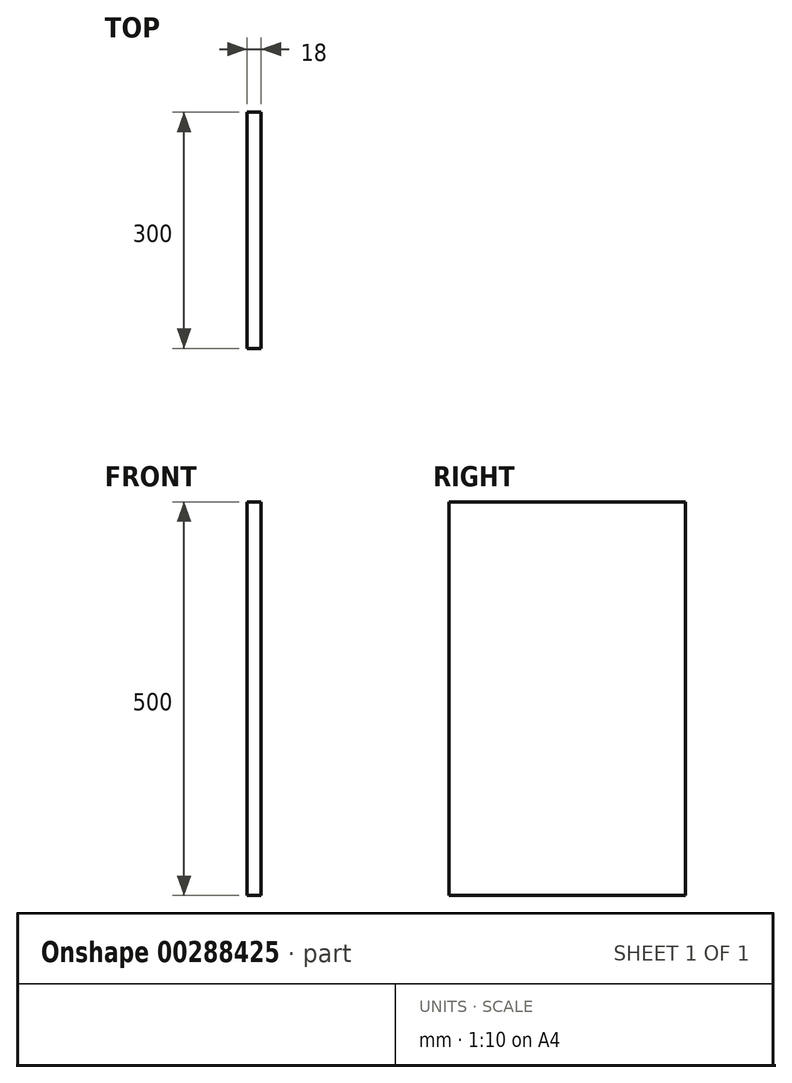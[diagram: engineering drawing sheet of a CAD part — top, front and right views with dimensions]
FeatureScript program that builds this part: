
annotation { "Feature Type Name" : "Feature", "Feature Type Description" : "" }
export const myFeature = defineFeature(function(context is Context, id is Id, definition is map)
    precondition{}
    {
        {
            var Q0;
            Q0=qCreatedBy(makeId("Front.planeOp"),FACE);
            var sketch = newSketch(context, id + "F0", { "sketchPlane" : qUnion([Q0])});
            skLineSegment(sketch, "E0.bottom", {"start": v(-71.06, 304.17) * mm, "end": v(-53.06, 304.17) * mm});
            skLineSegment(sketch, "E0.top", {"start": v(-71.06, -195.83) * mm, "end": v(-53.06, -195.83) * mm});
            skLineSegment(sketch, "E0.left", {"start": v(-71.06, 304.17) * mm, "end": v(-71.06, -195.83) * mm});
            skLineSegment(sketch, "E0.right", {"start": v(-53.06, 304.17) * mm, "end": v(-53.06, -195.83) * mm});
            skSolve(sketch);
        }
        {
            var Q0;
            Q0 = qSketchRegion(id + "F0", true);
            var Q1;
            Q1=makeQuery(id+"F0.imprint","IMPRINT",FACE,{"disambiguationData":[TD([[makeQuery(id+"F0.imprint","IMPRINT",EDGE,{"derivedFrom":sQuery(id+"F0.wireOp",EDGE,"E0.bottom")}),-1.0]])]});
            extrude(context, id + "F1", {"entities" : qUnion([Q0, Q1]), "depth" : 300 * mm});
        }
    });
